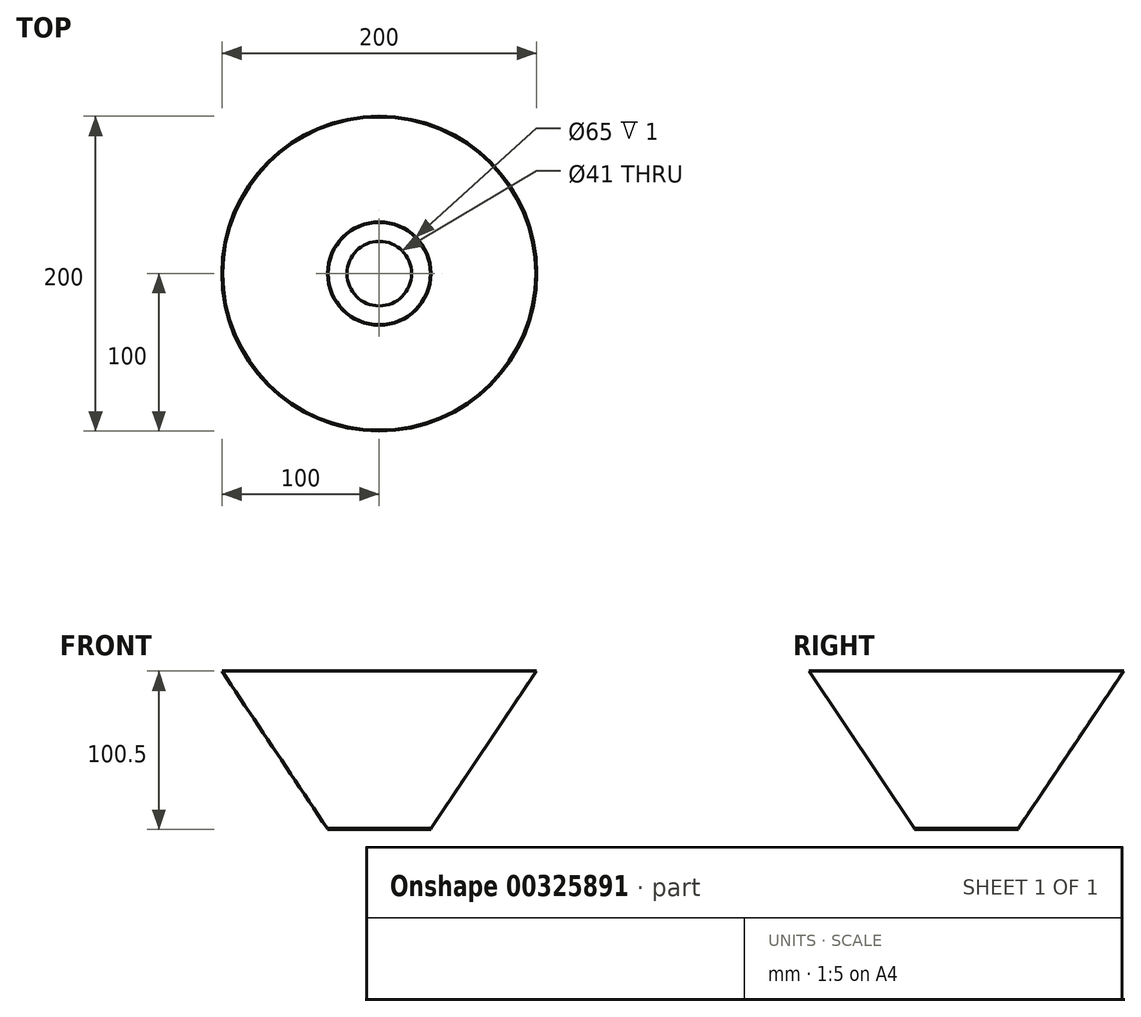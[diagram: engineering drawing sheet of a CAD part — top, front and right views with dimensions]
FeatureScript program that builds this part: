
annotation { "Feature Type Name" : "Feature", "Feature Type Description" : "" }
export const myFeature = defineFeature(function(context is Context, id is Id, definition is map)
    precondition{}
    {
        {
            var Q0;
            Q0=qCreatedBy(makeId("Top.planeOp"),FACE);
            var sketch = newSketch(context, id + "F0", { "sketchPlane" : qUnion([Q0])});
            skCircle(sketch, "E0", {"center": v(0, 0) * mm, "radius": 20.5 * mm});
            skCircle(sketch, "E1", {"center": v(0, 0) * mm, "radius": 32.5 * mm});
            skSolve(sketch);
        }
        {
            var Q0;
            Q0=qCreatedBy(makeId("Front.planeOp"),FACE);
            var sketch = newSketch(context, id + "F1", { "sketchPlane" : qUnion([Q0])});
            skLineSegment(sketch, "E2.0", {"start": v(-32.5, 0) * mm, "end": v(32.5, 0) * mm});
            skLineSegment(sketch, "E3", {"start": v(32.5, 0) * mm, "end": v(99.5, 100) * mm});
            skLineSegment(sketch, "E4", {"start": v(32.5, 0) * mm, "end": v(33, 0) * mm});
            skLineSegment(sketch, "E5", {"start": v(33, 0) * mm, "end": v(100, 100) * mm});
            skLineSegment(sketch, "E6", {"start": v(99.5, 100) * mm, "end": v(100, 100) * mm});
            skLineSegment(sketch, "E7.bottom", {"start": v(33, 0) * mm, "end": v(32.5, 0) * mm});
            skLineSegment(sketch, "E7.top", {"start": v(33, -0.5) * mm, "end": v(32.5, -0.5) * mm});
            skLineSegment(sketch, "E7.left", {"start": v(33, 0) * mm, "end": v(33, -0.5) * mm});
            skLineSegment(sketch, "E7.right", {"start": v(32.5, 0) * mm, "end": v(32.5, -0.5) * mm});
            skLineSegment(sketch, "E8.left", {"start": v(33, 0) * mm, "end": v(33, 0) * mm});
            skLineSegment(sketch, "E8.right", {"start": v(32.5, 0) * mm, "end": v(32.5, 0) * mm});
            skLineSegment(sketch, "E9.top", {"start": v(32.5, 0.5) * mm, "end": v(33, 0.5) * mm});
            skLineSegment(sketch, "E9.left", {"start": v(32.5, 0) * mm, "end": v(32.5, 0.5) * mm});
            skLineSegment(sketch, "E9.right", {"start": v(33, 0) * mm, "end": v(33, 0.5) * mm});
            skPoint(sketch, "E10", {"position": v(-100, 100) * mm});
            skSolve(sketch);
        }
        {
            var Q0;
            Q0 = qSketchRegion(id + "F1", true);
            var Q1;
            Q1=sQuery(id+"F0.wireOp",EDGE,"E1");
            revolve(context, id + "F2", {"entities" : qUnion([Q0]), "axis" : qUnion([Q1]), "revolveType" : RevolveType.FULL});
        }
        {
            var Q0;
            Q0 = qSketchRegion(id + "F0", true);
            extrude(context, id + "F3", {"entities" : qUnion([Q0]), "endBound" : BoundingType.SYMMETRIC, "depth" : 1 * mm});
        }
    });
